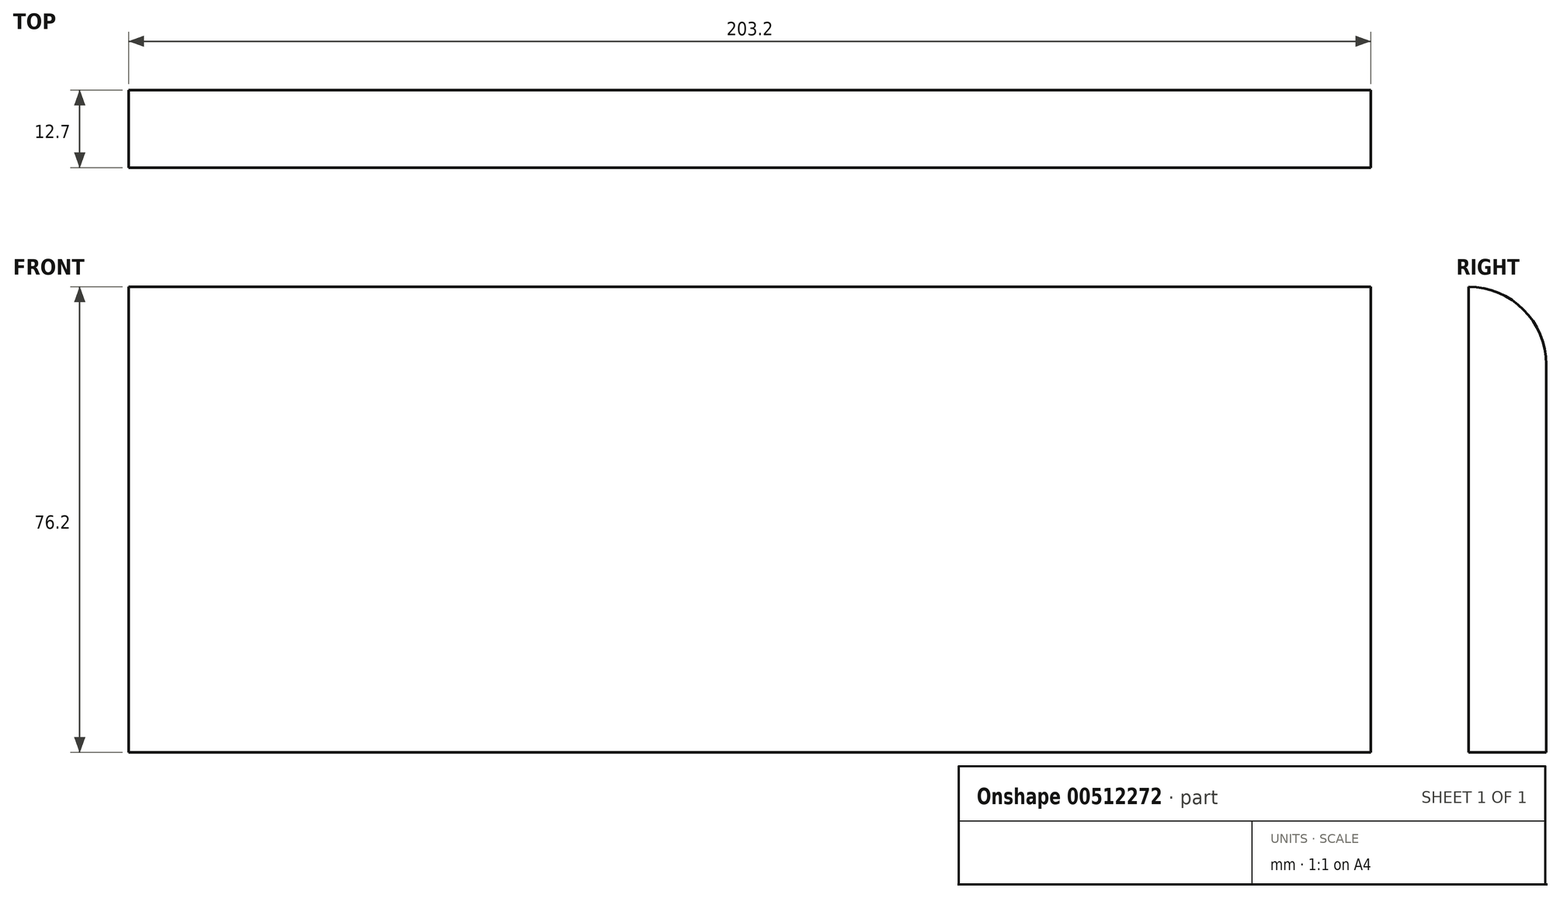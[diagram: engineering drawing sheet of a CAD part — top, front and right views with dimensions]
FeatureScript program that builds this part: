
annotation { "Feature Type Name" : "Feature", "Feature Type Description" : "" }
export const myFeature = defineFeature(function(context is Context, id is Id, definition is map)
    precondition{}
    {
        {
            var Q0;
            Q0=qCreatedBy(makeId("Front.planeOp"),FACE);
            var sketch = newSketch(context, id + "F0", { "sketchPlane" : qUnion([Q0])});
            skLineSegment(sketch, "E0.bottom", {"start": v(-101.6, 38.1) * mm, "end": v(101.6, 38.1) * mm});
            skLineSegment(sketch, "E0.top", {"start": v(-101.6, -38.1) * mm, "end": v(101.6, -38.1) * mm});
            skLineSegment(sketch, "E0.left", {"start": v(-101.6, 38.1) * mm, "end": v(-101.6, -38.1) * mm});
            skLineSegment(sketch, "E0.right", {"start": v(101.6, 38.1) * mm, "end": v(101.6, -38.1) * mm});
            skSolve(sketch);
        }
        {
            var Q0;
            Q0=makeQuery(id+"F0.imprint","IMPRINT",FACE,{"disambiguationData":[TD([[makeQuery(id+"F0.imprint","IMPRINT",EDGE,{"derivedFrom":sQuery(id+"F0.wireOp",EDGE,"E0.bottom")}),-1.0]])]});
            extrude(context, id + "F1", {"entities" : qUnion([Q0]), "depth" : 12.7 * mm});
        }
        {
            var Q0;
            Q0=makeQuery(id+"F1.opExtrude","CAP_EDGE",EDGE,{"disambiguationData":[OSD([sQuery(id+"F0.wireOp",EDGE,"E0.bottom")])],"isStart":true});
            fillet(context, id + "F2", {"entities" : qUnion([Q0]), "radius" : 12.7 * mm, "tangentPropagation" : true, "allowEdgeOverflow" : false});
        }
    });
